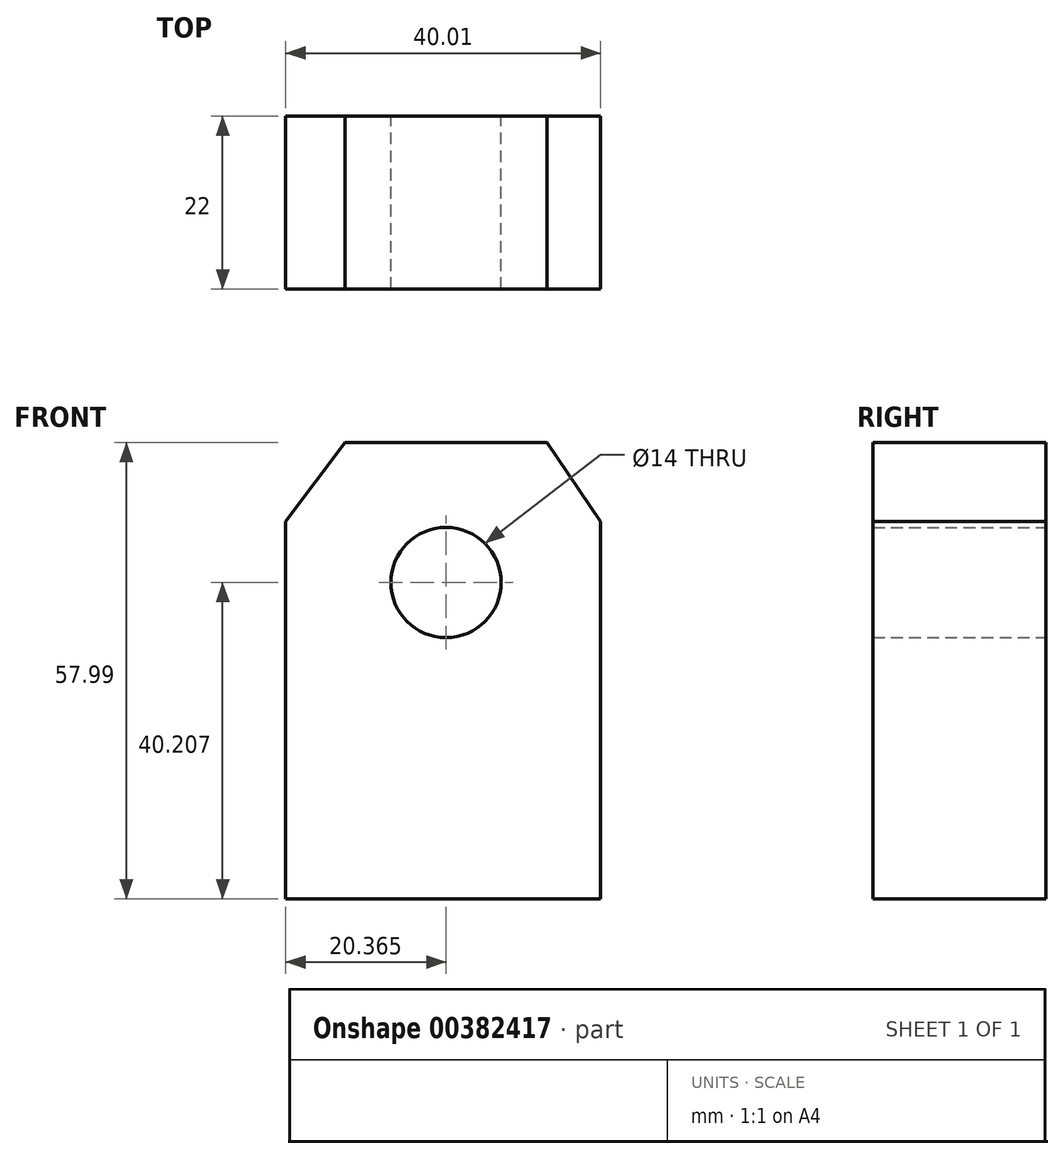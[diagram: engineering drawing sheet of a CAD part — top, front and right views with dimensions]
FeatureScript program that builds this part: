
annotation { "Feature Type Name" : "Feature", "Feature Type Description" : "" }
export const myFeature = defineFeature(function(context is Context, id is Id, definition is map)
    precondition{}
    {
        {
            var Q0;
            Q0=qCreatedBy(makeId("Front.planeOp"),FACE);
            var sketch = newSketch(context, id + "F0", { "sketchPlane" : qUnion([Q0])});
            skLineSegment(sketch, "E0", {"start": v(-33.19, 28.03) * mm, "end": v(-33.19, -19.95) * mm});
            skLineSegment(sketch, "E1", {"start": v(-33.19, -19.95) * mm, "end": v(6.82, -19.95) * mm});
            skLineSegment(sketch, "E2", {"start": v(6.82, -19.95) * mm, "end": v(6.82, 28.03) * mm});
            skLineSegment(sketch, "E3", {"start": v(6.82, 28.03) * mm, "end": v(0, 38.04) * mm});
            skLineSegment(sketch, "E4", {"start": v(0, 38.04) * mm, "end": v(-25.63, 38.04) * mm});
            skLineSegment(sketch, "E5", {"start": v(-25.63, 38.04) * mm, "end": v(-33.19, 28.03) * mm});
            skCircle(sketch, "E6", {"center": v(-12.82, 20.26) * mm, "radius": 7 * mm});
            skSolve(sketch);
        }
        {
            var Q0;
            Q0 = qSketchRegion(id + "F0", true);
            extrude(context, id + "F1", {"entities" : qUnion([Q0]), "depth" : 22 * mm});
        }
    });
